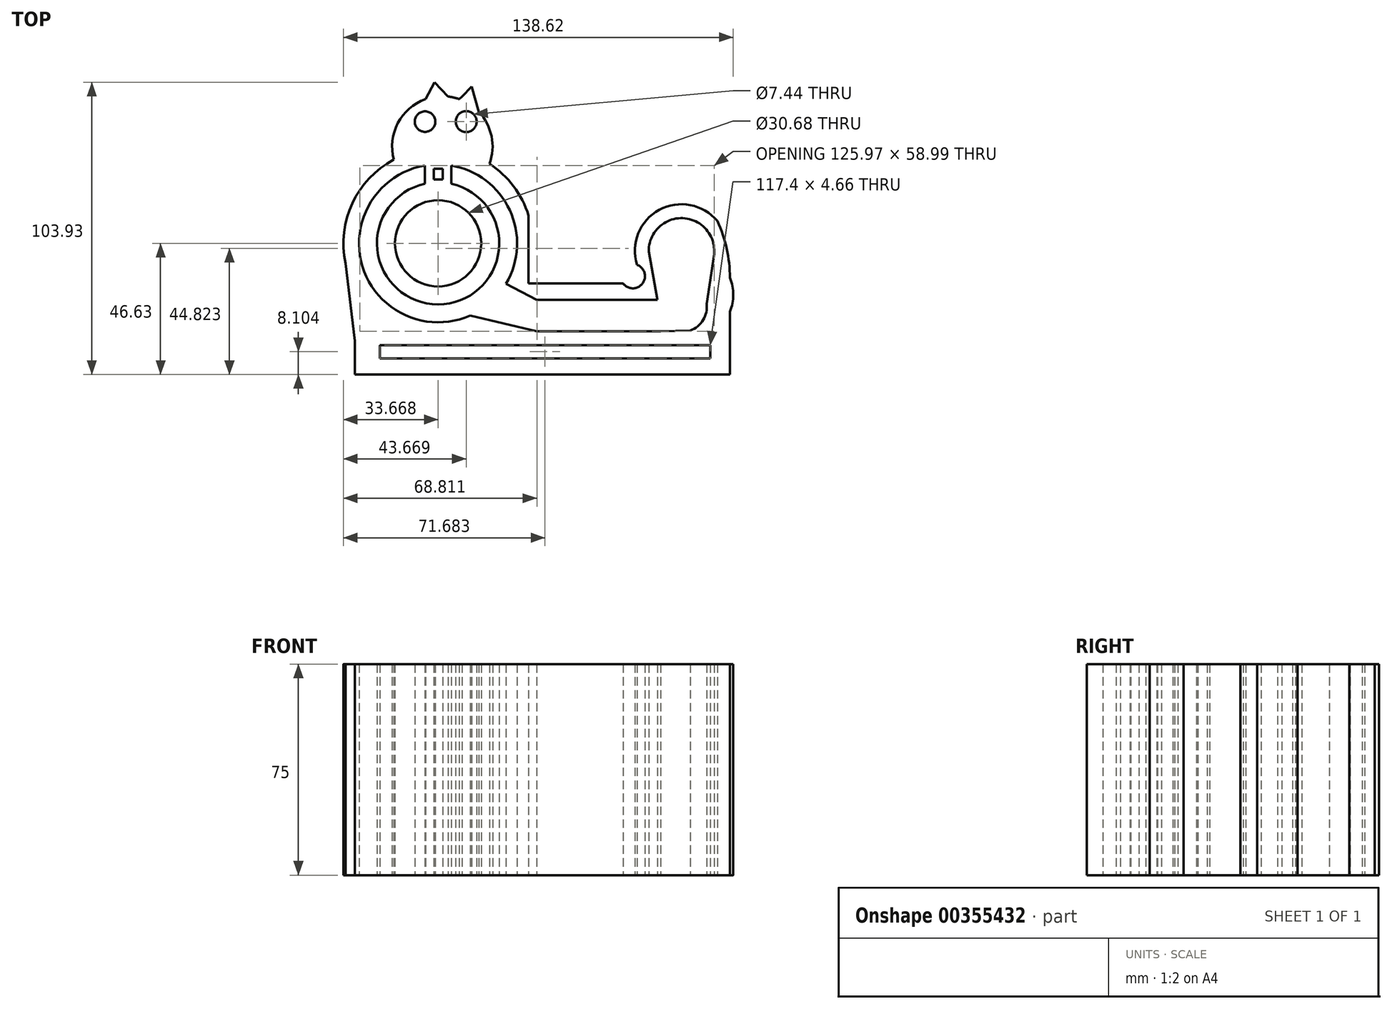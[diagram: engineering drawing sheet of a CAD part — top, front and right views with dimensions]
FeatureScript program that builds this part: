
annotation { "Feature Type Name" : "Feature", "Feature Type Description" : "" }
export const myFeature = defineFeature(function(context is Context, id is Id, definition is map)
    precondition{}
    {
        {
            var Q0;
            Q0=qCreatedBy(makeId("Top.planeOp"),FACE);
            var sketch = newSketch(context, id + "F0", { "sketchPlane" : qUnion([Q0])});
            skArc(sketch, "E0", {"start": v(-61.77, 55.08) * mm, "mid": v(-71.6, 46.53) * mm, "end": v(-73.02, 33.58) * mm});
            skLineSegment(sketch, "E1", {"start": v(-61.77, 55.08) * mm, "end": v(-58.52, 61.11) * mm});
            skLineSegment(sketch, "E2", {"start": v(-58.52, 61.11) * mm, "end": v(-53.72, 56) * mm});
            skPoint(sketch, "E3.start.orphan", {"position": v(-48.77, 56) * mm});
            skLineSegment(sketch, "E4", {"start": v(-48.77, 56) * mm, "end": v(-45.42, 59.59) * mm});
            skLineSegment(sketch, "E5", {"start": v(-45.42, 59.59) * mm, "end": v(-42.83, 50.56) * mm});
            skLineSegment(sketch, "E6", {"start": v(-48.77, 56) * mm, "end": v(-50.14, 54.7) * mm});
            skArc(sketch, "E7.trimOffspring", {"start": v(-49.76, 55.07) * mm, "mid": v(-51.7, 55.64) * mm, "end": v(-53.72, 56) * mm});
            skArc(sketch, "E8", {"start": v(-73.02, 33.58) * mm, "mid": v(-88.11, 17.38) * mm, "end": v(-89.88, -4.7) * mm});
            skArc(sketch, "E9.trimOffspring", {"start": v(-39.02, 32.08) * mm, "mid": v(-38.29, 41.86) * mm, "end": v(-42.83, 50.56) * mm});
            skArc(sketch, "E10.trimOffspring", {"start": v(-25.14, 13.74) * mm, "mid": v(-30.46, 24.13) * mm, "end": v(-39.02, 32.08) * mm});
            skArc(sketch, "E11.trimOffspring", {"start": v(34, -31.08) * mm, "mid": v(34.16, -30.56) * mm, "end": v(34.33, -30.04) * mm});
            skArc(sketch, "E12", {"start": v(46.46, -20.46) * mm, "mid": v(47.65, -14.45) * mm, "end": v(46.46, -8.43) * mm});
            skArc(sketch, "E13", {"start": v(41.98, 11.73) * mm, "mid": v(21.3, 15.7) * mm, "end": v(13.4, -3.81) * mm});
            skArc(sketch, "E14.trimOffspring", {"start": v(16.76, -9.8) * mm, "mid": v(16.66, -10.15) * mm, "end": v(16.57, -10.5) * mm});
            skPoint(sketch, "E15.firstSnap0", {"position": v(26.48, 17.48) * mm});
            skPoint(sketch, "E15.oppositeSnap0", {"position": v(46.46, -20.46) * mm});
            skLineSegment(sketch, "E16.trimOffspring", {"start": v(46.46, -20.46) * mm, "end": v(46.46, -30.94) * mm});
            skCircle(sketch, "E17", {"center": v(-61.93, 47.1) * mm, "radius": 3.65 * mm});
            skCircle(sketch, "E18", {"center": v(-47.3, 47.1) * mm, "radius": 3.72 * mm});
            skArc(sketch, "E19", {"start": v(-61.97, 31.5) * mm, "mid": v(-84.18, -4.32) * mm, "end": v(-45.83, -21.82) * mm});
            skArc(sketch, "E20", {"start": v(-61.97, 25.03) * mm, "mid": v(-57.32, -17.91) * mm, "end": v(-52.6, 25.02) * mm});
            skPoint(sketch, "E15.left.start.orphan", {"position": v(26.48, 11.73) * mm});
            skLineSegment(sketch, "E21.bottom", {"start": v(-22.24, -16.3) * mm, "end": v(20.63, -16.3) * mm});
            skLineSegment(sketch, "E21.top", {"start": v(-22.24, -27.5) * mm, "end": v(21.76, -27.5) * mm});
            skArc(sketch, "E22", {"start": v(40.82, 0) * mm, "mid": v(29.69, 12.76) * mm, "end": v(17.59, 0.9) * mm});
            skLineSegment(sketch, "E23", {"start": v(21.76, -27.5) * mm, "end": v(32.41, -27.17) * mm});
            skArc(sketch, "E24.trimOffspring", {"start": v(32.41, -27.17) * mm, "mid": v(36.97, -23.43) * mm, "end": v(38.17, -17.66) * mm});
            skLineSegment(sketch, "E25", {"start": v(17.59, 0.9) * mm, "end": v(20.63, -16.3) * mm});
            skLineSegment(sketch, "E26", {"start": v(40.82, 0) * mm, "end": v(38.17, -17.66) * mm});
            skLineSegment(sketch, "E27", {"start": v(-78.1, -32.39) * mm, "end": v(-77.99, -32.39) * mm});
            skLineSegment(sketch, "E28", {"start": v(-33.14, -10.5) * mm, "end": v(-22.24, -16.3) * mm});
            skLineSegment(sketch, "E29", {"start": v(-45.83, -21.82) * mm, "end": v(-22.24, -27.5) * mm});
            skArc(sketch, "E30.trimOffspring", {"start": v(-33.14, -10.5) * mm, "mid": v(-31.83, 15.63) * mm, "end": v(-52.64, 31.5) * mm});
            skLineSegment(sketch, "E31", {"start": v(-25.14, 13.74) * mm, "end": v(-25.14, -10.5) * mm});
            skLineSegment(sketch, "E32", {"start": v(-25.14, -10.5) * mm, "end": v(8.51, -10.5) * mm});
            skLineSegment(sketch, "E33", {"start": v(-63.55, 41.4) * mm, "end": v(-63.55, 41.4) * mm});
            skPoint(sketch, "E34.start.orphan", {"position": v(-65.35, 39.6) * mm});
            skPoint(sketch, "E35.center.orphan", {"position": v(-57.43, 35.22) * mm});
            skPoint(sketch, "E36.start.orphan", {"position": v(-56.27, 35.22) * mm});
            skLineSegment(sketch, "E37.top", {"start": v(46.46, -42.82) * mm, "end": v(-86.94, -42.82) * mm});
            skLineSegment(sketch, "E37.left", {"start": v(46.46, -30.94) * mm, "end": v(46.46, -42.82) * mm});
            skLineSegment(sketch, "E37.right", {"start": v(-86.94, -30.94) * mm, "end": v(-86.94, -42.82) * mm});
            skPoint(sketch, "E38.orphan", {"position": v(-71.03, -32.39) * mm});
            skLineSegment(sketch, "E39", {"start": v(-90.21, -3.3) * mm, "end": v(-86.94, -30.94) * mm});
            skCircle(sketch, "E40", {"center": v(-57.3, 3.81) * mm, "radius": 15.34 * mm});
            skPoint(sketch, "E41.oppositeSnap0", {"position": v(-52.6, 28.04) * mm});
            skLineSegment(sketch, "E41.left", {"start": v(-61.97, 31.5) * mm, "end": v(-61.97, 25.02) * mm});
            skLineSegment(sketch, "E41.right", {"start": v(-52.6, 31.5) * mm, "end": v(-52.6, 25.02) * mm});
            skArc(sketch, "E42.trimOffspring", {"start": v(-52.6, 31.4) * mm, "mid": v(-52.62, 31.45) * mm, "end": v(-52.64, 31.5) * mm});
            skPoint(sketch, "E43.centerSnap0", {"position": v(12.54, -10.5) * mm});
            skLineSegment(sketch, "E44.bottom", {"start": v(-77.99, -32.39) * mm, "end": v(39.41, -32.39) * mm});
            skLineSegment(sketch, "E44.top", {"start": v(-77.99, -37.05) * mm, "end": v(39.41, -37.05) * mm});
            skLineSegment(sketch, "E44.left", {"start": v(-77.99, -32.39) * mm, "end": v(-77.99, -37.05) * mm});
            skLineSegment(sketch, "E44.right", {"start": v(39.41, -32.39) * mm, "end": v(39.41, -37.05) * mm});
            skLineSegment(sketch, "E45.bottom", {"start": v(-58.85, 30.38) * mm, "end": v(-55.65, 30.38) * mm});
            skLineSegment(sketch, "E45.top", {"start": v(-58.85, 26.52) * mm, "end": v(-55.65, 26.52) * mm});
            skLineSegment(sketch, "E45.left", {"start": v(-58.85, 30.38) * mm, "end": v(-58.85, 26.52) * mm});
            skLineSegment(sketch, "E45.right", {"start": v(-55.65, 30.38) * mm, "end": v(-55.65, 26.52) * mm});
            skArc(sketch, "E46", {"start": v(8.51, -10.5) * mm, "mid": v(15.4, -10.4) * mm, "end": v(13.4, -3.81) * mm});
            skArc(sketch, "E47", {"start": v(46.46, -8.43) * mm, "mid": v(45.32, 1.9) * mm, "end": v(41.98, 11.73) * mm});
            skSolve(sketch);
        }
        {
            var Q0;
            Q0 = qSketchRegion(id + "F0", true);
            extrude(context, id + "F1", {"entities" : qUnion([Q0]), "depth" : 75 * mm});
        }
    });
